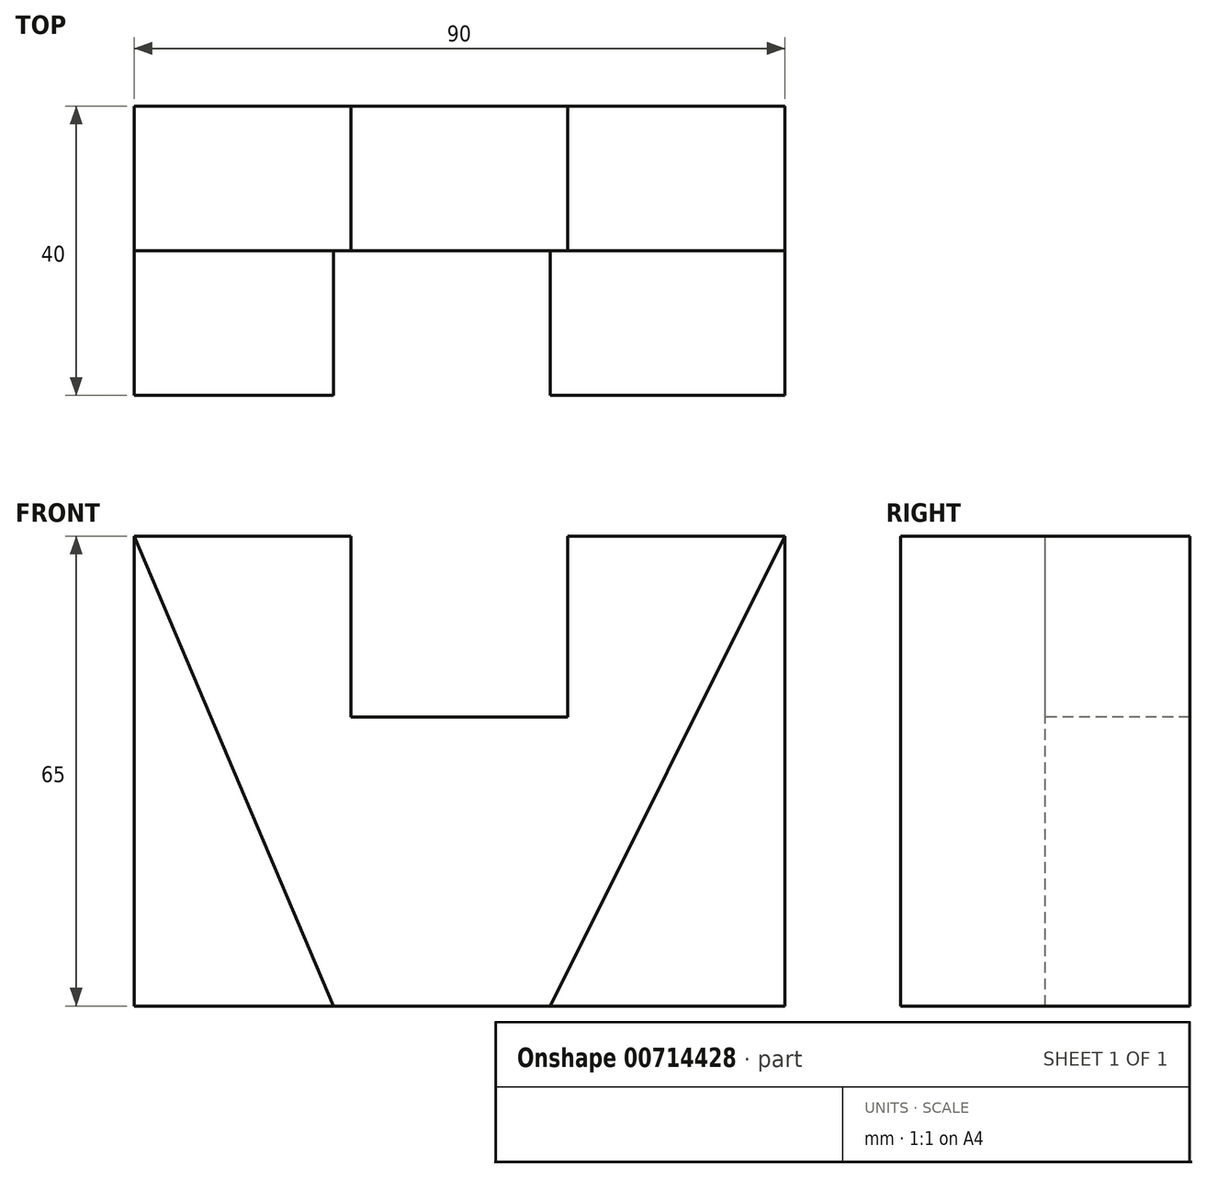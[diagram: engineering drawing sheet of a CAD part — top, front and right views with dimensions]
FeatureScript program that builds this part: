
annotation { "Feature Type Name" : "Feature", "Feature Type Description" : "" }
export const myFeature = defineFeature(function(context is Context, id is Id, definition is map)
    precondition{}
    {
        {
            var Q0;
            Q0=qCreatedBy(makeId("Front.planeOp"),FACE);
            var sketch = newSketch(context, id + "F0", { "sketchPlane" : qUnion([Q0])});
            skLineSegment(sketch, "E0.bottom", {"start": v(45, -32.5) * mm, "end": v(-45, -32.5) * mm});
            skLineSegment(sketch, "E0.top", {"start": v(45, 32.5) * mm, "end": v(-45, 32.5) * mm});
            skLineSegment(sketch, "E0.left", {"start": v(45, -32.5) * mm, "end": v(45, 32.5) * mm});
            skLineSegment(sketch, "E0.right", {"start": v(-45, -32.5) * mm, "end": v(-45, 32.5) * mm});
            skPoint(sketch, "E0.middle", {"position": v(0, 0) * mm});
            skSolve(sketch);
        }
        {
            var Q0;
            Q0=makeQuery(id+"F0.imprint","IMPRINT",FACE,{"disambiguationData":[TD([[makeQuery(id+"F0.imprint","IMPRINT",EDGE,{"derivedFrom":sQuery(id+"F0.wireOp",EDGE,"E0.bottom")}),-1.0]])]});
            extrude(context, id + "F1", {"entities" : qUnion([Q0]), "depth" : 40 * mm, "offsetDistance" : 25 * mm});
        }
        {
            var Q0;
            Q0=makeQuery(id+"F1.opExtrude","CAP_FACE",FACE,{"disambiguationData":[OSD([sQuery(id+"F0.wireOp",EDGE,"E0.bottom"),sQuery(id+"F0.wireOp",EDGE,"E0.top"),sQuery(id+"F0.wireOp",EDGE,"E0.left"),sQuery(id+"F0.wireOp",EDGE,"E0.right")])],"isStart":false});
            var sketch = newSketch(context, id + "F2", { "sketchPlane" : qUnion([Q0])});
            skLineSegment(sketch, "E1", {"start": v(-17.42, -32.5) * mm, "end": v(-45, 32.5) * mm});
            skLineSegment(sketch, "E2", {"start": v(12.58, -32.5) * mm, "end": v(45, 32.5) * mm});
            skSolve(sketch);
        }
        {
            var Q0;
            {var subQ0=sQuery(id+"F2.wireOp",EDGE,"E1");Q0=makeQuery(id+"F2.imprint","IMPRINT",FACE,{"disambiguationData":[TD([[makeQuery(id+"F2.imprint","IMPRINT",EDGE,{"derivedFrom":subQ0}),-1.0]])]});}
            extrude(context, id + "F3", {"entities" : qUnion([Q0]), "operationType" : NewBodyOperationType.REMOVE, "oppositeDirection" : true, "depth" : 20 * mm, "offsetDistance" : 25 * mm});
        }
        {
            var Q0;
            Q0=makeQuery(id+"F3.boolean.opBoolean","COPY",FACE,{"derivedFrom":makeQuery(id+"F3.opExtrude","CAP_FACE",FACE,{"disambiguationData":[OSD([sQuery(id+"F0.wireOp",EDGE,"E0.bottom"),sQuery(id+"F0.wireOp",EDGE,"E0.top"),sQuery(id+"F2.wireOp",EDGE,"E1"),sQuery(id+"F2.wireOp",EDGE,"E2")])],"isStart":false})});
            var sketch = newSketch(context, id + "F4", { "sketchPlane" : qUnion([Q0])});
            skLineSegment(sketch, "E3.bottom", {"start": v(15, 7.5) * mm, "end": v(-15, 7.5) * mm});
            skLineSegment(sketch, "E3.top", {"start": v(15, 57.5) * mm, "end": v(-15, 57.5) * mm});
            skLineSegment(sketch, "E3.left", {"start": v(15, 7.5) * mm, "end": v(15, 57.5) * mm});
            skLineSegment(sketch, "E3.right", {"start": v(-15, 7.5) * mm, "end": v(-15, 57.5) * mm});
            skPoint(sketch, "E3.middle", {"position": v(0, 32.5) * mm});
            skSolve(sketch);
        }
        {
            var Q0;
            {var subQ0=sQuery(id+"F4.wireOp",EDGE,"E3.bottom");Q0=makeQuery(id+"F4.imprint","IMPRINT",FACE,{"disambiguationData":[TD([[makeQuery(id+"F4.imprint","IMPRINT",EDGE,{"derivedFrom":subQ0}),-1.0]])]});}
            var Q1;
            {var subQ0=sQuery(id+"F4.wireOp",EDGE,"E3.top");Q1=makeQuery(id+"F4.imprint","IMPRINT",FACE,{"disambiguationData":[TD([[makeQuery(id+"F4.imprint","IMPRINT",EDGE,{"derivedFrom":subQ0}),1.0]])]});}
            extrude(context, id + "F5", {"entities" : qUnion([Q0, Q1]), "operationType" : NewBodyOperationType.REMOVE, "endBound" : BoundingType.THROUGH_ALL, "oppositeDirection" : true, "depth" : 25 * mm, "offsetDistance" : 25 * mm});
        }
    });
